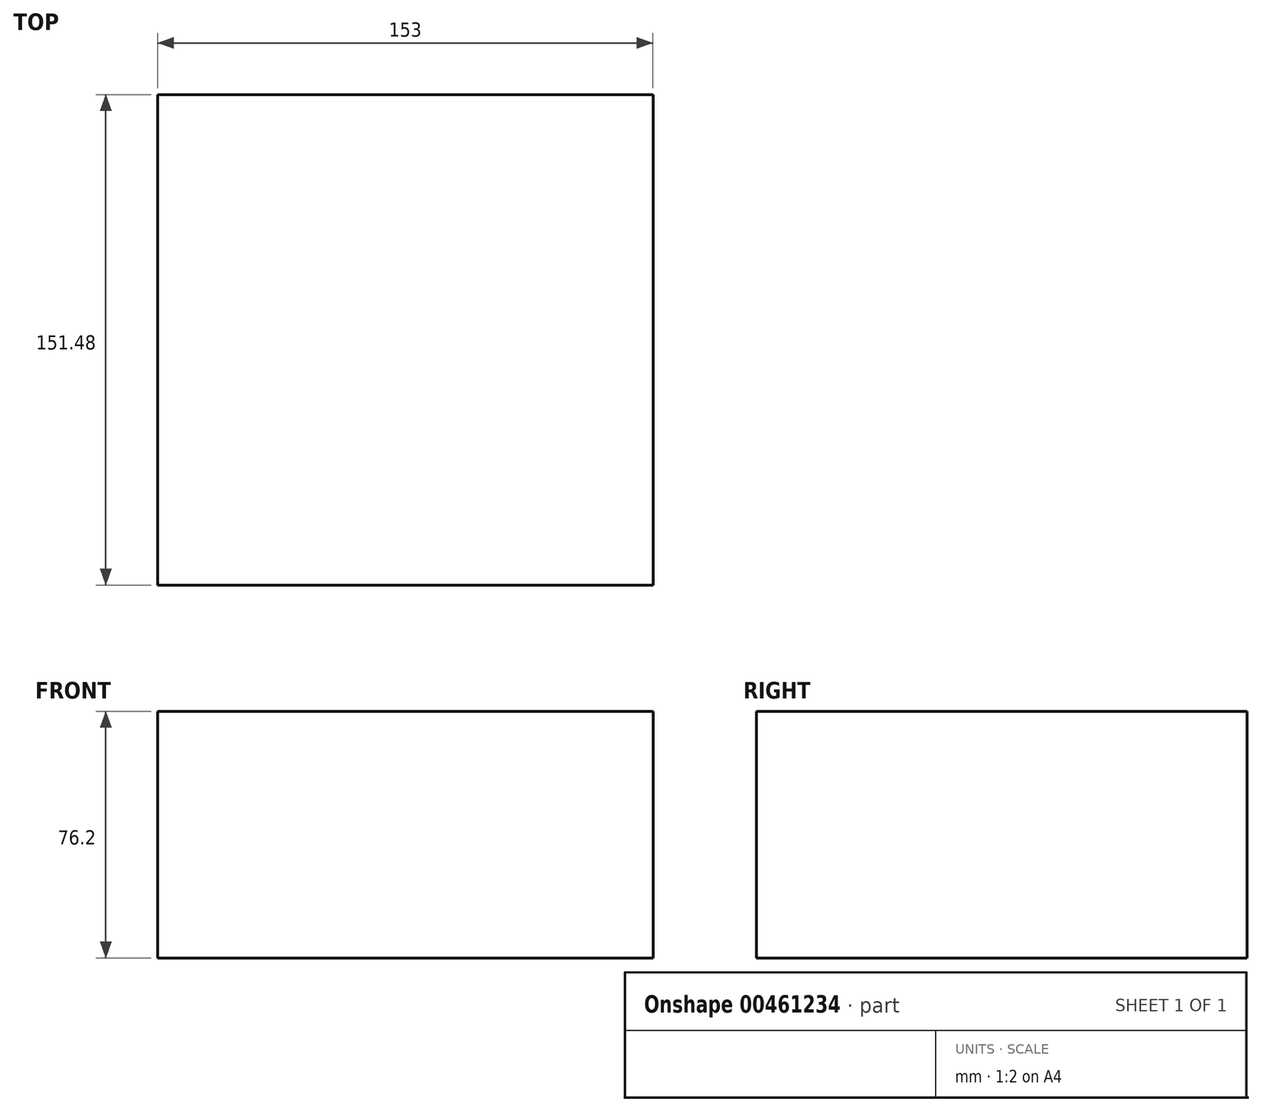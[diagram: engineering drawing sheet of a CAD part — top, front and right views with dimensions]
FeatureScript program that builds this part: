
annotation { "Feature Type Name" : "Feature", "Feature Type Description" : "" }
export const myFeature = defineFeature(function(context is Context, id is Id, definition is map)
    precondition{}
    {
        {
            var Q0;
            Q0=qCreatedBy(makeId("Top.planeOp"),FACE);
            var sketch = newSketch(context, id + "F0", { "sketchPlane" : qUnion([Q0])});
            skLineSegment(sketch, "E0.bottom", {"start": v(76.5, 75.74) * mm, "end": v(-76.5, 75.74) * mm});
            skLineSegment(sketch, "E0.top", {"start": v(76.5, -75.74) * mm, "end": v(-76.5, -75.74) * mm});
            skLineSegment(sketch, "E0.left", {"start": v(76.5, 75.74) * mm, "end": v(76.5, -75.74) * mm});
            skLineSegment(sketch, "E0.right", {"start": v(-76.5, 75.74) * mm, "end": v(-76.5, -75.74) * mm});
            skPoint(sketch, "E0.middle", {"position": v(0, 0) * mm});
            skSolve(sketch);
        }
        {
            var Q0;
            Q0 = qSketchRegion(id + "F0", true);
            extrude(context, id + "F1", {"entities" : qUnion([Q0]), "depth" : 76.2 * mm});
        }
    });
